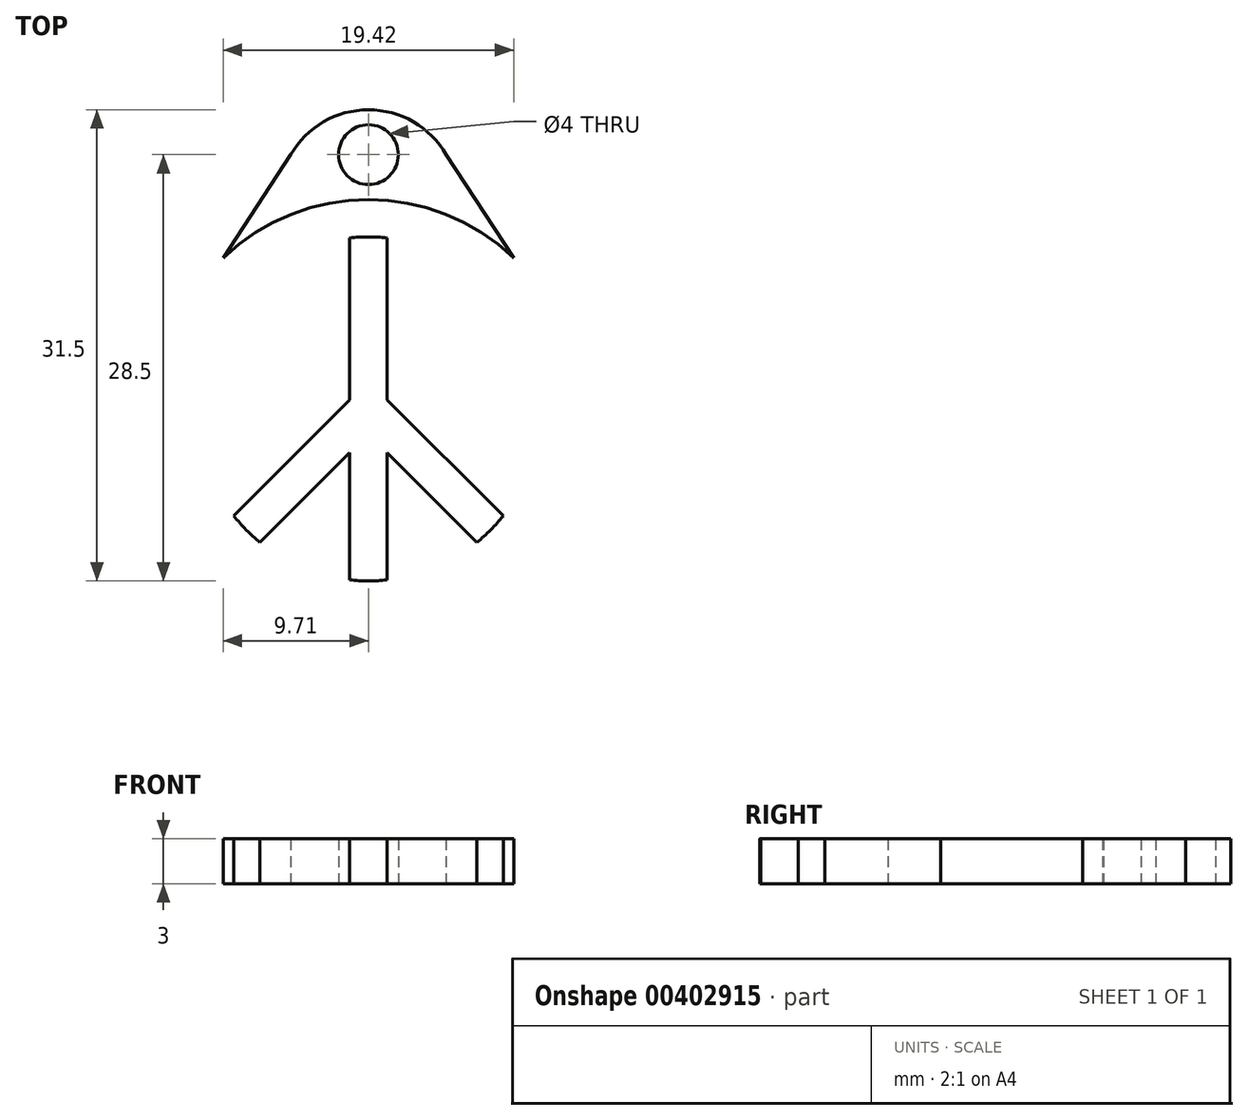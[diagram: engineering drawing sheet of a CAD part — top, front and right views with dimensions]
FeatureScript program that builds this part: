
annotation { "Feature Type Name" : "Feature", "Feature Type Description" : "" }
export const myFeature = defineFeature(function(context is Context, id is Id, definition is map)
    precondition{}
    {
        {
            var Q0;
            Q0=qCreatedBy(makeId("Top.planeOp"),FACE);
            var sketch = newSketch(context, id + "F0", { "sketchPlane" : qUnion([Q0])});
            skCircle(sketch, "E0", {"center": v(0, 0) * mm, "radius": 14 * mm});
            skLineSegment(sketch, "E1", {"start": v(0, 14) * mm, "end": v(0, -14) * mm, "construction": true});
            skLineSegment(sketch, "E2", {"start": v(-11.07, -8.57) * mm, "end": v(-2, 0.5) * mm});
            skLineSegment(sketch, "E3", {"start": v(-8.16, -11.38) * mm, "end": v(-2, -5.22) * mm});
            skLineSegment(sketch, "E4", {"start": v(-6.54, -4.04) * mm, "end": v(-3.68, -6.9) * mm, "construction": true});
            skLineSegment(sketch, "E5", {"start": v(-5.1, -5.46) * mm, "end": v(-9.72, -10.08) * mm, "construction": true});
            skLineSegment(sketch, "E6", {"start": v(-5.1, -5.46) * mm, "end": v(0, -0.36) * mm, "construction": true});
            skLineSegment(sketch, "E7", {"start": v(-2, 13.86) * mm, "end": v(-2, 0.5) * mm});
            skLineSegment(sketch, "E8", {"start": v(-2, 0.5) * mm, "end": v(-2, -5.22) * mm, "construction": true});
            skLineSegment(sketch, "E9", {"start": v(-2, -5.22) * mm, "end": v(-2, -13.86) * mm});
            skLineSegment(sketch, "E10", {"start": v(0, 0) * mm, "end": v(-2, 0) * mm, "construction": true});
            skLineSegment(sketch, "E11.MirrorCS", {"start": v(2, -5.22) * mm, "end": v(2, -13.86) * mm});
            skLineSegment(sketch, "E12.MirrorCS", {"start": v(8.16, -11.38) * mm, "end": v(2, -5.22) * mm});
            skLineSegment(sketch, "E13.MirrorCS", {"start": v(11.07, -8.57) * mm, "end": v(2, 0.5) * mm});
            skLineSegment(sketch, "E14.MirrorCS", {"start": v(2, 13.86) * mm, "end": v(2, 0.5) * mm});
            skCircle(sketch, "E15", {"center": v(0, 0) * mm, "radius": 15 * mm});
            skSolve(sketch);
        }
        {
            var Q0;
            Q0=qCreatedBy(makeId("Top.planeOp"),FACE);
            var sketch = newSketch(context, id + "F1", { "sketchPlane" : qUnion([Q0])});
            skLineSegment(sketch, "E16", {"start": v(-15, 0) * mm, "end": v(15, 0) * mm, "construction": true});
            skLineSegment(sketch, "E17", {"start": v(0, 0) * mm, "end": v(0, -15) * mm, "construction": true});
            skCircle(sketch, "E18", {"center": v(0, 0) * mm, "radius": 14 * mm});
            skCircle(sketch, "E19", {"center": v(0, 0) * mm, "radius": 11.5 * mm});
            skLineSegment(sketch, "E20", {"start": v(-9, -7.15) * mm, "end": v(-1.25, 0.6) * mm});
            skLineSegment(sketch, "E21", {"start": v(-1.25, 0.6) * mm, "end": v(-1.25, -2.93) * mm, "construction": true});
            skLineSegment(sketch, "E22", {"start": v(-1.25, -2.93) * mm, "end": v(-7.25, -8.93) * mm});
            skLineSegment(sketch, "E23", {"start": v(-5.13, -3.27) * mm, "end": v(-3.36, -5.04) * mm, "construction": true});
            skLineSegment(sketch, "E24", {"start": v(-4.25, -4.15) * mm, "end": v(-1.25, -1.16) * mm, "construction": true});
            skLineSegment(sketch, "E25", {"start": v(-1.25, -11.43) * mm, "end": v(-1.25, -2.93) * mm});
            skLineSegment(sketch, "E26", {"start": v(-1.25, 11.43) * mm, "end": v(-1.25, 0.6) * mm});
            skLineSegment(sketch, "E27.MirrorCS", {"start": v(9, -7.15) * mm, "end": v(1.25, 0.6) * mm});
            skLineSegment(sketch, "E28.MirrorCS", {"start": v(1.25, -2.93) * mm, "end": v(7.25, -8.93) * mm});
            skLineSegment(sketch, "E29.MirrorCS", {"start": v(1.25, -11.43) * mm, "end": v(1.25, -2.93) * mm});
            skLineSegment(sketch, "E30.MirrorCS", {"start": v(1.25, 11.43) * mm, "end": v(1.25, 0.6) * mm});
            skLineSegment(sketch, "E31", {"start": v(0, 0) * mm, "end": v(0, 14) * mm, "construction": true});
            skArc(sketch, "E32", {"start": v(5.86, 12.71) * mm, "mid": v(0, 20) * mm, "end": v(-5.86, 12.71) * mm});
            skCircle(sketch, "E33", {"center": v(0, 17) * mm, "radius": 2 * mm});
            skLineSegment(sketch, "E34", {"start": v(0, 17) * mm, "end": v(0, 14) * mm, "construction": true});
            skLineSegment(sketch, "E35", {"start": v(9.71, 10.08) * mm, "end": v(5.2, 17) * mm});
            skLineSegment(sketch, "E36.MirrorCS", {"start": v(-9.71, 10.08) * mm, "end": v(-5.2, 17) * mm});
            skLineSegment(sketch, "E37", {"start": v(-5.2, 17) * mm, "end": v(5.2, 17) * mm, "construction": true});
            skLineSegment(sketch, "E38", {"start": v(0, 17) * mm, "end": v(0, 19) * mm, "construction": true});
            skSolve(sketch);
        }
        {
            var Q0;
            {var subQ3=sQuery(id+"F1.wireOp",EDGE,"E20");Q0=makeQuery(id+"F1.imprint","IMPRINT",FACE,{"disambiguationData":[TD([[makeQuery(id+"F1.imprint","IMPRINT",EDGE,{"derivedFrom":subQ3}),-1.0]])]});}
            var Q1;
            {var subQ0=sQuery(id+"F1.wireOp",EDGE,"E19");var subQ13=makeQuery(id+"F1.imprint","IMPRINT",VERTEX,{"derivedFrom":subQ0});Q1=makeQuery(id+"F1.imprint","IMPRINT",FACE,{"disambiguationData":[TD([[makeQuery(id+"F1.imprint","IMPRINT",EDGE,{"disambiguationData":[TD([[subQ13,-1.0]])],"derivedFrom":subQ0}),-1.0]])]});}
            var Q2;
            {var subQ0=sQuery(id+"F1.wireOp",EDGE,"E32");Q2=makeQuery(id+"F1.imprint","IMPRINT",FACE,{"disambiguationData":[TD([[makeQuery(id+"F1.imprint","IMPRINT",EDGE,{"derivedFrom":subQ0}),1.0]])]});}
            var Q3;
            {var subQ0=sQuery(id+"F1.wireOp",EDGE,"E36.MirrorCS");Q3=makeQuery(id+"F1.imprint","IMPRINT",FACE,{"disambiguationData":[TD([[makeQuery(id+"F1.imprint","IMPRINT",EDGE,{"derivedFrom":subQ0}),-1.0]])]});}
            var Q4;
            {var subQ0=sQuery(id+"F1.wireOp",EDGE,"E35");Q4=makeQuery(id+"F1.imprint","IMPRINT",FACE,{"disambiguationData":[TD([[makeQuery(id+"F1.imprint","IMPRINT",EDGE,{"derivedFrom":subQ0}),1.0]])]});}
            extrude(context, id + "F2", {"entities" : qUnion([Q0, Q1, Q2, Q3, Q4]), "depth" : 3 * mm, "offsetDistance" : 25 * mm});
        }
    });
